# Revit family: L-PLT_소나무(장송)
name_source: partatom
category: 수목
units: mm (PartAtom-declared; Revit-internal decimal feet)

## family parameters
OmniClass 번호 = 23.40.05.00
OmniClass 제목 = Plants and Planting Products
공유 = 아니오
렌더 모양 소스 = 패밀리 형상
로드될 때 보이드를 사용하여 절단 = 아니오
작업 기준면 기반 = 아니오
항상 수직 = 예

## types (4) — shared parameters
KBIMS_보급정보-저작자 = 림인포테크_MMJ
LIM_INFO_PL_구분 = 상록교목
LIM_INFO_PL_수목단위 = 주
LIM_INFO_PL_품명 = 소나무(장송)
LIM_INFO_PL_학명 = Pinus densiflora Siebold & Zucc.
LIM_INFO_버전 = 2022_V01
LIM_INFO_제작일 = 20211210
LIM_INFO_주의사항 = 재배포, 재가공, 판매 금지
R = 200
건설정보분류체계-부위분류 = E985
뿌리분 높이 = 545
뿌리분 직경 = 1090
조달청표준공사코드-세부공종 = 10161599224940
콘 높이 = 273
zero-valued in all types: LIM_INFO_PL_M2당수량, LIM_INFO_PL_가격, LIM_INFO_PL_주당인정수량

## per-type parameters (varying)
| type | H | LIM_INFO_PL_규격 | 높이 |
| 소나무(장송) H10.0 X 60R | 10000  [stored 32.8084 ft] | H10.0 X 60R | 10000  [stored 32.8084 ft] |
| 소나무(장송) H10.0 X 45R | 10000  [stored 32.8084 ft] | H10.0 X 45R | 10000  [stored 32.8084 ft] |
| 소나무(장송) 9.0H X 35R | 9000 | 9.0H X 35R | 9000 |
| 소나무(장송) 8.0H X 25R | 8000 | 8.0H X 25R | 8000 |

note: [stored X ft] marks values corroborated as IEEE doubles in the binary element streams (Revit-internal decimal feet)
